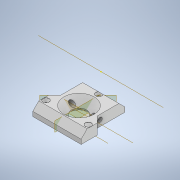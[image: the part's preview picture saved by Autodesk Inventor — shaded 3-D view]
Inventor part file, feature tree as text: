
AUTODESK INVENTOR PART (.ipt)
format: ipt  version: 2022 (Build 260153000, 153)  size: 259,072 bytes
history: native  units: mm
features: sketch x11, extrude x8, plane x6, projected_geometry x6, other x6, reference x3, hole x2, chamfer x1
ambient origin geometry x8: Origin, YZ Plane, XZ Plane, XY Plane, X Axis, Y Axis, Z Axis, Center Point
bodies: Volumenkörper1 (feature_tree)
feature tree (43):
  extrude  "Extrusion1"  Depth=28.0mm
  plane  "Arbeitsebene2"
  plane  "Arbeitsebene3"
  extrude  "Extrusion6"  Depth=5.0mm
  plane  "Arbeitsebene4"
  sketch  "Skizze7"  dims[d25=6.0mm d26=0.0mm d27=3.0mm]
  extrude  "Extrusion7"  Depth=3.0mm
  plane  "Arbeitsebene5"
  extrude  "Extrusion9"  Depth=7.0mm TaperAngle=0.0deg
  plane  "Arbeitsebene6"
  hole  "Bohrung3"  [1 undecoded]
  extrude  "Extrusion10"  Depth=1.8mm
  extrude  "Extrusion11"  Depth=10.0mm TaperAngle=0.0deg
  hole  "Bohrung2"  [1 undecoded]
  chamfer  "Fase3"  Distance=2.0mm
  extrude  "Extrusion12"  Depth=5.0mm
  extrude  "Extrusion13"  [1 undecoded]
  sketch  "Skizze1"  dims[d0=18.0mm d1=28.0mm]
  plane  "Arbeitsebene1"
  sketch  "Skizze6"  dims[d2=7.0mm d3=0.0mm d24=5.0mm]
  projected_geometry  "Projizierte Kontur6"
  sketch  "Skizze8"  dims[d28=3.0mm d29=7.0mm d30=0.0mm]
  projected_geometry  "Projizierte Kontur7"
  sketch  "Skizze10"  dims[d38=2.9mm d39=0.0mm d40=0.0mm]
  projected_geometry  "Projizierte Kontur8"
  sketch  "Skizze13"  dims[d48=4.0mm d49=6.0mm d50=4.0mm d51=2.0mm d52=90.0deg d53=0.1mm d54=20.594885mm d55=1.8mm]
  sketch  "Skizze14"  dims[d56=1.8mm d57=6.0mm d58=4.0mm d59=4.0mm d60=90.0deg d61=10.0mm d62=20.594885mm d63=4.0mm d64=0.0mm]
  sketch  "Skizze15"  dims[d65=4.0mm d66=0.0mm d67=4.0mm d68=2.0mm d69=45.0deg]
  projected_geometry  "Projizierte Kontur12"
  sketch  "Skizze16"  dims[d70=12.7mm d71=2.0mm d72=0.0mm]
  projected_geometry  "Projizierte Kontur13"
  reference  "Referenz1"
  reference  "Referenz2"
  reference  "Referenz4"
  sketch  "Sketch17"  dims[d73=20.0mm d74=5.0mm d75=-7.853982mm]
  projected_geometry  "Projected Loop14"
  sketch  "Sketch18"
  other  "Assembly_Cube_Fibercombiner_v3.iam"
  other  "DIN 912 - ersetzt durch DIN EN ISO 4762 M3 x 25:3"
  other  "DIN 912 - ersetzt durch DIN EN ISO 4762 M3 x 25:1"
  other  "DIN 912 - ersetzt durch DIN EN ISO 4762 M3 x 25:2"
  other  "Assembly_Cube_empty_IM_v3:2"
  other  "10_Cube_1x1_IM:1"
note: 3 required parameter values undecoded (feature->parameter linkage not recoverable at this tier; creation-order binding heuristic only, values carry confidence <= 0.55)
